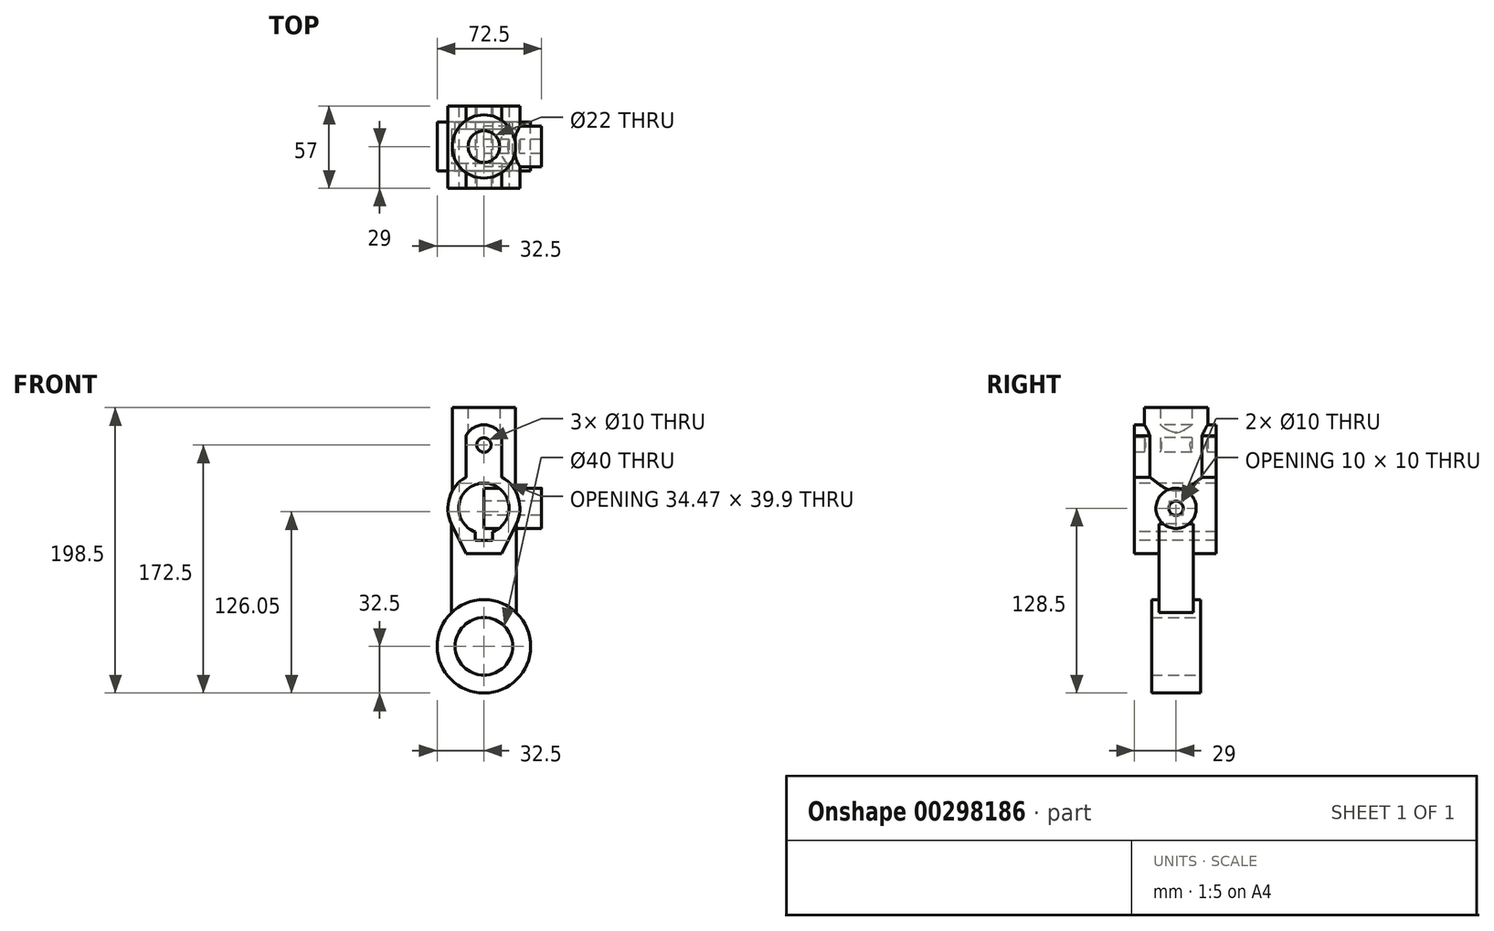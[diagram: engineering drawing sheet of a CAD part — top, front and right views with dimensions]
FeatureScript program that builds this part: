
annotation { "Feature Type Name" : "Feature", "Feature Type Description" : "" }
export const myFeature = defineFeature(function(context is Context, id is Id, definition is map)
    precondition{}
    {
        {
            var Q0;
            Q0=qCreatedBy(makeId("Front.planeOp"),FACE);
            var sketch = newSketch(context, id + "F0", { "sketchPlane" : qUnion([Q0])});
            skCircle(sketch, "E0", {"center": v(0, 0) * mm, "radius": 32.5 * mm});
            skCircle(sketch, "E1", {"center": v(0, 0) * mm, "radius": 20 * mm});
            skSolve(sketch);
        }
        {
            var Q0;
            Q0=makeQuery(id+"F0.imprint","IMPRINT",FACE,{"disambiguationData":[TD([[makeQuery(id+"F0.imprint","IMPRINT",EDGE,{"derivedFrom":sQuery(id+"F0.wireOp",EDGE,"E0")}),1.0]])]});
            extrude(context, id + "F1", {"entities" : qUnion([Q0]), "endBound" : BoundingType.SYMMETRIC, "depth" : 34 * mm});
        }
        {
            var Q0;
            Q0=qCreatedBy(makeId("Front.planeOp"),FACE);
            var sketch = newSketch(context, id + "F2", { "sketchPlane" : qUnion([Q0])});
            skLineSegment(sketch, "E2", {"start": v(-22.5, 23.45) * mm, "end": v(-22.5, 96) * mm});
            skLineSegment(sketch, "E3", {"start": v(-22.5, 96) * mm, "end": v(22.5, 96) * mm});
            skLineSegment(sketch, "E4", {"start": v(22.5, 96) * mm, "end": v(22.5, 23.45) * mm});
            skArc(sketch, "E5", {"start": v(22.5, 23.45) * mm, "mid": v(0, 32.5) * mm, "end": v(-22.5, 23.45) * mm});
            skSolve(sketch);
        }
        {
            var Q0;
            Q0 = qSketchRegion(id + "F2", true);
            extrude(context, id + "F3", {"entities" : qUnion([Q0]), "operationType" : NewBodyOperationType.ADD, "endBound" : BoundingType.SYMMETRIC, "depth" : 24 * mm});
        }
        {
            var Q0;
            Q0=makeQuery(id+"F3.opExtrude","CAP_FACE",FACE,{"disambiguationData":[OSD([sQuery(id+"F2.wireOp",EDGE,"E2"),sQuery(id+"F2.wireOp",EDGE,"E3"),sQuery(id+"F2.wireOp",EDGE,"E4"),sQuery(id+"F2.wireOp",EDGE,"E5")])],"isStart":false});
            var sketch = newSketch(context, id + "F4", { "sketchPlane" : qUnion([Q0])});
            skLineSegment(sketch, "E6", {"start": v(12.5, 64.46) * mm, "end": v(22.5, 85.1) * mm});
            skLineSegment(sketch, "E7", {"start": v(-12.5, 64.46) * mm, "end": v(-22.5, 85.1) * mm});
            skArc(sketch, "E8", {"start": v(6, 79.56) * mm, "mid": v(0, 113.5) * mm, "end": v(-6, 79.56) * mm});
            skLineSegment(sketch, "E9", {"start": v(-6, 79.56) * mm, "end": v(-6, 73.6) * mm});
            skLineSegment(sketch, "E10", {"start": v(-6, 73.6) * mm, "end": v(6, 73.6) * mm});
            skLineSegment(sketch, "E11", {"start": v(6, 73.6) * mm, "end": v(6, 79.56) * mm});
            skLineSegment(sketch, "E12", {"start": v(12.5, 117.65) * mm, "end": v(12.5, 146.3) * mm});
            skArc(sketch, "E13", {"start": v(-12.5, 117.65) * mm, "mid": v(-23.9, 103.34) * mm, "end": v(-22.5, 85.1) * mm});
            skArc(sketch, "E14", {"start": v(22.5, 85.1) * mm, "mid": v(23.9, 103.34) * mm, "end": v(12.5, 117.65) * mm});
            skLineSegment(sketch, "E15", {"start": v(-12.5, 117.65) * mm, "end": v(-12.5, 146.3) * mm});
            skLineSegment(sketch, "E16", {"start": v(12.5, 64.46) * mm, "end": v(-12.5, 64.46) * mm});
            skCircle(sketch, "E17", {"center": v(0, 140) * mm, "radius": 5 * mm});
            skArc(sketch, "E18", {"start": v(12.5, 146.3) * mm, "mid": v(0, 154) * mm, "end": v(-12.5, 146.3) * mm});
            skSolve(sketch);
        }
        {
            var Q0;
            Q0=makeQuery(id+"F4.imprint","IMPRINT",FACE,{"disambiguationData":[TD([[makeQuery(id+"F4.imprint","IMPRINT",EDGE,{"derivedFrom":sQuery(id+"F4.wireOp",EDGE,"E12")}),1.0]])]});
            var Q1;
            {var subQ8=sQuery(id+"F4.wireOp",EDGE,"E6");Q1=makeQuery(id+"F4.imprint","IMPRINT",FACE,{"disambiguationData":[TD([[makeQuery(id+"F4.imprint","IMPRINT",EDGE,{"derivedFrom":subQ8}),1.0]])]});}
            extrude(context, id + "F5", {"entities" : qUnion([Q0, Q1]), "oppositeDirection" : true, "depth" : 40 * mm, "hasSecondDirection" : true, "secondDirectionOppositeDirection" : false, "secondDirectionDepth" : 17 * mm});
        }
        {
            var Q0;
            Q0=makeQuery(id+"F1.opExtrude","SWEPT_BODY",BODY,{"disambiguationData":[OSD([sQuery(id+"F0.wireOp",EDGE,"E0"),sQuery(id+"F0.wireOp",EDGE,"E1")])]});
            var Q1;
            Q1=makeQuery(id+"F5.opExtrude","SWEPT_BODY",BODY,{"disambiguationData":[OSD([sQuery(id+"F4.wireOp",EDGE,"E6"),sQuery(id+"F4.wireOp",EDGE,"E7"),sQuery(id+"F4.wireOp",EDGE,"E8"),sQuery(id+"F4.wireOp",EDGE,"E9"),sQuery(id+"F4.wireOp",EDGE,"E10"),sQuery(id+"F4.wireOp",EDGE,"E11"),sQuery(id+"F4.wireOp",EDGE,"E12"),sQuery(id+"F4.wireOp",EDGE,"E13"),sQuery(id+"F4.wireOp",EDGE,"E14"),sQuery(id+"F4.wireOp",EDGE,"E15"),sQuery(id+"F4.wireOp",EDGE,"E16"),sQuery(id+"F4.wireOp",EDGE,"E17"),sQuery(id+"F4.wireOp",EDGE,"E18")])]});
            booleanBodies(context, id + "F6", {"operationType" : BooleanOperationType.UNION, "tools" : qUnion([Q0, Q1])});
        }
        {
            var Q0;
            {var subQ0=sQuery(id+"F2.wireOp",EDGE,"E3");Q0=makeQuery(id+"F6.opBoolean","SPLIT",FACE,{"disambiguationData":[TD([makeQuery(id+"F3.opExtrude","SWEPT_FACE",FACE,{"disambiguationData":[OSD([subQ0])]})])],"derivedFrom":makeQuery(id+"F3.opExtrude","CAP_FACE",FACE,{"disambiguationData":[OSD([sQuery(id+"F2.wireOp",EDGE,"E2"),subQ0,sQuery(id+"F2.wireOp",EDGE,"E4"),sQuery(id+"F2.wireOp",EDGE,"E5")])],"isStart":false})});}
            var Q1;
            {var subQ0=sQuery(id+"FnkjfK8EGEifgpe_1.wireOp",EDGE,"JnLyO6YX-zvDT-h8LM-cqb1-DwfjRD713IfD.bottom");Q1=makeQuery(id+"FfVejzlmdzIJ6z0_1.boolean.opBoolean","SPLIT",FACE,{"disambiguationData":[TD([makeQuery(id+"F5.opExtrude","SWEPT_FACE",FACE,{"disambiguationData":[OSD([sQuery(id+"F4.wireOp",EDGE,"E8")])]})])],"derivedFrom":makeQuery(id+"FfVejzlmdzIJ6z0_1.opExtrude","CAP_FACE",FACE,{"disambiguationData":[OSD([subQ0,sQuery(id+"FnkjfK8EGEifgpe_1.wireOp",EDGE,"JnLyO6YX-zvDT-h8LM-cqb1-DwfjRD713IfD.top"),sQuery(id+"FnkjfK8EGEifgpe_1.wireOp",EDGE,"JnLyO6YX-zvDT-h8LM-cqb1-DwfjRD713IfD.left"),sQuery(id+"FnkjfK8EGEifgpe_1.wireOp",EDGE,"JnLyO6YX-zvDT-h8LM-cqb1-DwfjRD713IfD.right")])],"isStart":true})});}
            extrude(context, id + "F7", {"entities" : qUnion([Q0, Q1]), "operationType" : NewBodyOperationType.REMOVE, "endBound" : BoundingType.THROUGH_ALL, "oppositeDirection" : true, "depth" : 25 * mm});
        }
        {
            var Q0;
            Q0=makeQuery(id+"F5.opExtrude","SWEPT_FACE",FACE,{"disambiguationData":[OSD([sQuery(id+"F4.wireOp",EDGE,"E14")])]});
            cPlane(context, id + "F8", {"entities" : qUnion([Q0]), "cplaneType" : CPlaneType.LINE_ANGLE, "offset" : 25 * mm, "angle" : 0 * degree, "width" : 150 * mm, "height" : 150 * mm});
        }
        {
            var Q0;
            Q0=qCreatedBy(id+"F8.planeOp",FACE);
            var sketch = newSketch(context, id + "F9", { "sketchPlane" : qUnion([Q0])});
            skCircle(sketch, "E19", {"center": v(0, 0) * mm, "radius": 22 * mm});
            skCircle(sketch, "E20", {"center": v(0, 0) * mm, "radius": 11 * mm});
            skSolve(sketch);
        }
        {
            var Q0;
            Q0 = qSketchRegion(id + "F9", true);
            extrude(context, id + "F10", {"entities" : qUnion([Q0]), "operationType" : NewBodyOperationType.ADD, "oppositeDirection" : true, "depth" : 70 * mm});
        }
        {
            var Q0;
            Q0=makeQuery(id+"F5.opExtrude","CAP_FACE",FACE,{"disambiguationData":[OSD([sQuery(id+"F4.wireOp",EDGE,"E6"),sQuery(id+"F4.wireOp",EDGE,"E7"),sQuery(id+"F4.wireOp",EDGE,"E8"),sQuery(id+"F4.wireOp",EDGE,"E9"),sQuery(id+"F4.wireOp",EDGE,"E10"),sQuery(id+"F4.wireOp",EDGE,"E11"),sQuery(id+"F4.wireOp",EDGE,"E12"),sQuery(id+"F4.wireOp",EDGE,"E13"),sQuery(id+"F4.wireOp",EDGE,"E14"),sQuery(id+"F4.wireOp",EDGE,"E15"),sQuery(id+"F4.wireOp",EDGE,"E16"),sQuery(id+"F4.wireOp",EDGE,"E17"),sQuery(id+"F4.wireOp",EDGE,"E18")])],"isStart":true});
            var sketch = newSketch(context, id + "F11", { "sketchPlane" : qUnion([Q0])});
            skLineSegment(sketch, "E21", {"start": v(-17.5, 96) * mm, "end": v(17.5, 96) * mm});
            skArc(sketch, "E22", {"start": v(17.5, 96) * mm, "mid": v(0, 113.5) * mm, "end": v(-17.5, 96) * mm});
            skSolve(sketch);
        }
        {
            var Q0;
            Q0 = qSketchRegion(id + "F11", true);
            extrude(context, id + "F12", {"entities" : qUnion([Q0]), "operationType" : NewBodyOperationType.REMOVE, "endBound" : BoundingType.THROUGH_ALL, "oppositeDirection" : true, "depth" : 25 * mm});
        }
        {
            var Q0;
            Q0=qCreatedBy(makeId("Right.planeOp"),FACE);
            var sketch = newSketch(context, id + "F13", { "sketchPlane" : qUnion([Q0])});
            skCircle(sketch, "E23", {"center": v(0, 96) * mm, "radius": 14 * mm});
            skCircle(sketch, "E24", {"center": v(0, 96) * mm, "radius": 5 * mm});
            skSolve(sketch);
        }
        {
            var Q0;
            Q0 = qSketchRegion(id + "F13", true);
            extrude(context, id + "F14", {"entities" : qUnion([Q0]), "operationType" : NewBodyOperationType.ADD, "depth" : 40 * mm});
        }
    });
